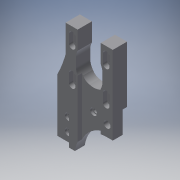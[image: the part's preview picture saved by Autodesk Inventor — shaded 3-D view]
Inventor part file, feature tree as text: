
AUTODESK INVENTOR PART (.ipt)
format: ipt  version: 2018 (Build 220112000, 112)  size: 516,608 bytes
history: native  units: in
note: dims shown in document units (in); Inventor stores cm internally (conversion verified against a paired STEP export)
features: extrude x13, sketch x13, projected_geometry x5, fillet x3, plane x2
ambient origin geometry x8: Origin, YZ Plane, XZ Plane, XY Plane, X Axis, Y Axis, Z Axis, Center Point
bodies: Solid1 (feature_tree)
feature tree (36):
  extrude  "Extrusion1"  Depth=1.6929in
  extrude  "Extrusion2"  Depth=0.4331in
  fillet  "Fillet1"  Radius=1.6535in
  extrude  "Extrusion3"  Depth=1.2205in
  extrude  "Extrusion4"  Depth=0.126in
  extrude  "Extrusion5"  Depth=0.315in
  plane  "Work Plane1"
  plane  "Work Plane2"
  extrude  "Extrusion9"  Depth=0.2362in TaperAngle=0.0deg
  sketch  "Sketch12"  dims[d15=0.315in d16=0.1575in d17=0.0in]
  extrude  "Extrusion13"  Depth=0.1575in TaperAngle=0.0deg
  extrude  "Extrusion14"  Depth=0.2362in
  extrude  "Extrusion15"  Depth=0.0787in
  extrude  "Extrusion16"  Depth=0.6102in
  extrude  "Extrusion17"  Depth=0.2165in
  extrude  "Extrusion18"  Depth=0.3937in
  extrude  "Extrusion19"  Depth=0.0787in
  fillet  "Fillet5"  Radius=4.2606in
  fillet  "Fillet6"  Radius=0.3937in
  sketch  "Sketch1"  dims[d0=3.8189in d1=1.6929in]
  sketch  "Sketch2"  dims[d2=0.4331in d3=0.4331in d4=1.6535in]
  sketch  "Sketch3"  dims[d5=0.1969in d6=0.0in d7=1.2205in]
  projected_geometry  "Projected Loop1"
  sketch  "Sketch4"  dims[d8=1.2205in d9=0.126in]
  projected_geometry  "Projected Loop2"
  sketch  "Sketch5"  dims[d10=0.2756in d11=0.315in]
  projected_geometry  "Projected Loop3"
  sketch  "Sketch10"  dims[d12=0.315in d13=0.2362in d14=0.0in]
  projected_geometry  "Projected Loop4"
  sketch  "Sketch14"  dims[d18=0.2362in d20=0.2362in]
  sketch  "Sketch15"  dims[d21=0.0787in d22=0.0in d23=0.9449in]
  sketch  "Sketch16"  dims[d24=0.315in d25=0.6102in]
  sketch  "Sketch17"  dims[d26=0.0in d27=0.0in d43=0.2165in]
  sketch  "Sketch18"  dims[d44=0.1654in d47=0.3937in]
  sketch  "Sketch19"  dims[d50=0.2362in d51=0.0in d69=1.2992in d70=4.2606in d71=0.3937in d72=0.0in d73=0.1181in d74=1.063in d75=7.0866in d76=0.3937in d77=0.0in d78=0.2047in d79=0.2441in d80=0.2362in d81=0.0in d82=0.3937in d83=0.1654in d84=0.1654in d85=0.315in d86=0.4724in d87=0.2362in d88=0.0in d89=0.2441in d91=0.0787in d92=0.0in d93=0.7874in d94=0.3937in d95=0.0787in d96=0.0in d97=0.3937in d98=0.1575in d99=0.0in d100=0.0787in d101=0.0787in]
  projected_geometry  "Projected Loop5"
